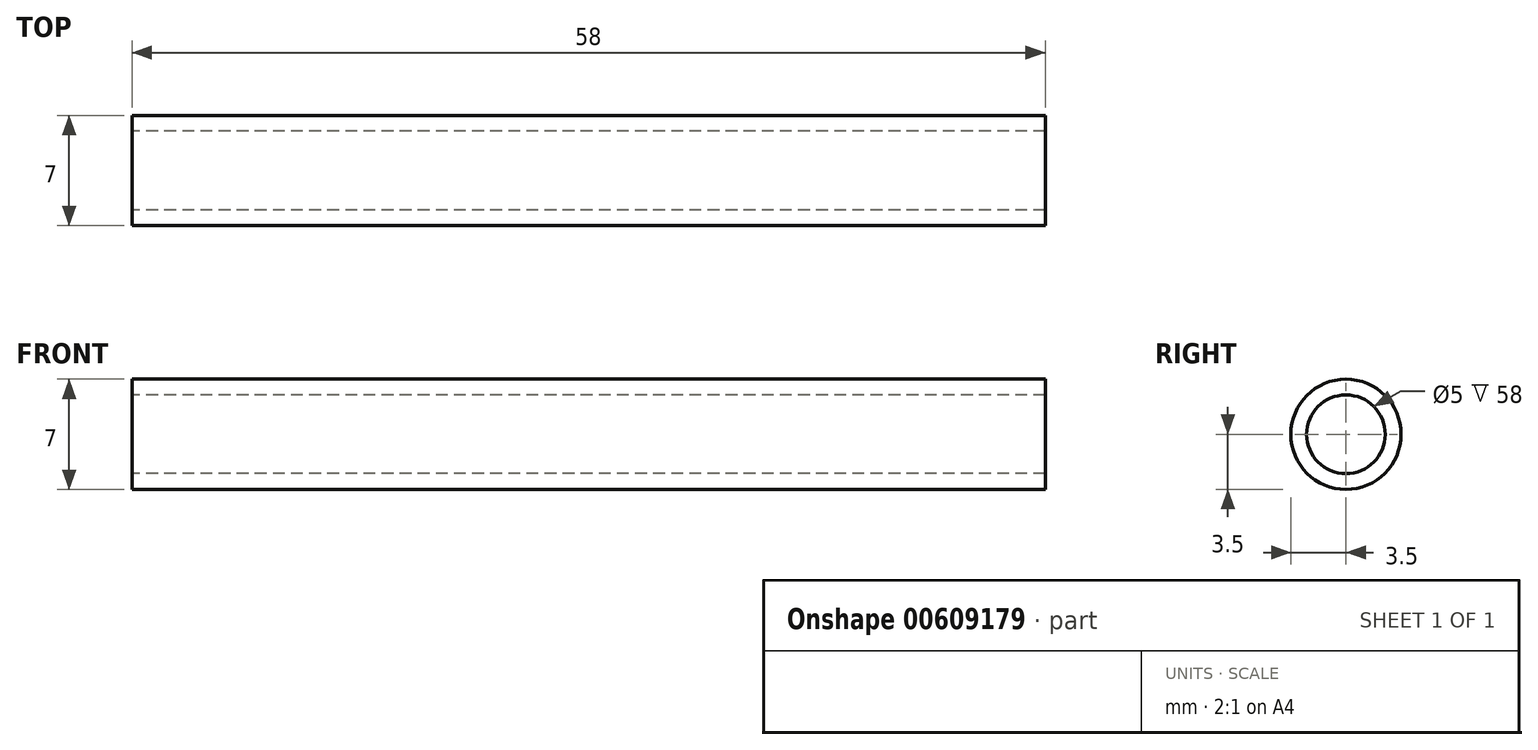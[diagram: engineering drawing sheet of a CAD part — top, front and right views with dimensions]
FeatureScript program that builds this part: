
annotation { "Feature Type Name" : "Feature", "Feature Type Description" : "" }
export const myFeature = defineFeature(function(context is Context, id is Id, definition is map)
    precondition{}
    {
        {
            var Q0;
            Q0=qCreatedBy(makeId("Right.planeOp"),FACE);
            var sketch = newSketch(context, id + "F0", { "sketchPlane" : qUnion([Q0])});
            skCircle(sketch, "E0", {"center": v(0, 0) * mm, "radius": 2.5 * mm});
            skCircle(sketch, "E1.0", {"center": v(0, 0) * mm, "radius": 3.5 * mm});
            skSolve(sketch);
        }
        {
            var Q0;
            Q0 = qSketchRegion(id + "F0", true);
            extrude(context, id + "F1", {"entities" : qUnion([Q0]), "depth" : 58 * mm, "offsetDistance" : 25 * mm});
        }
    });
